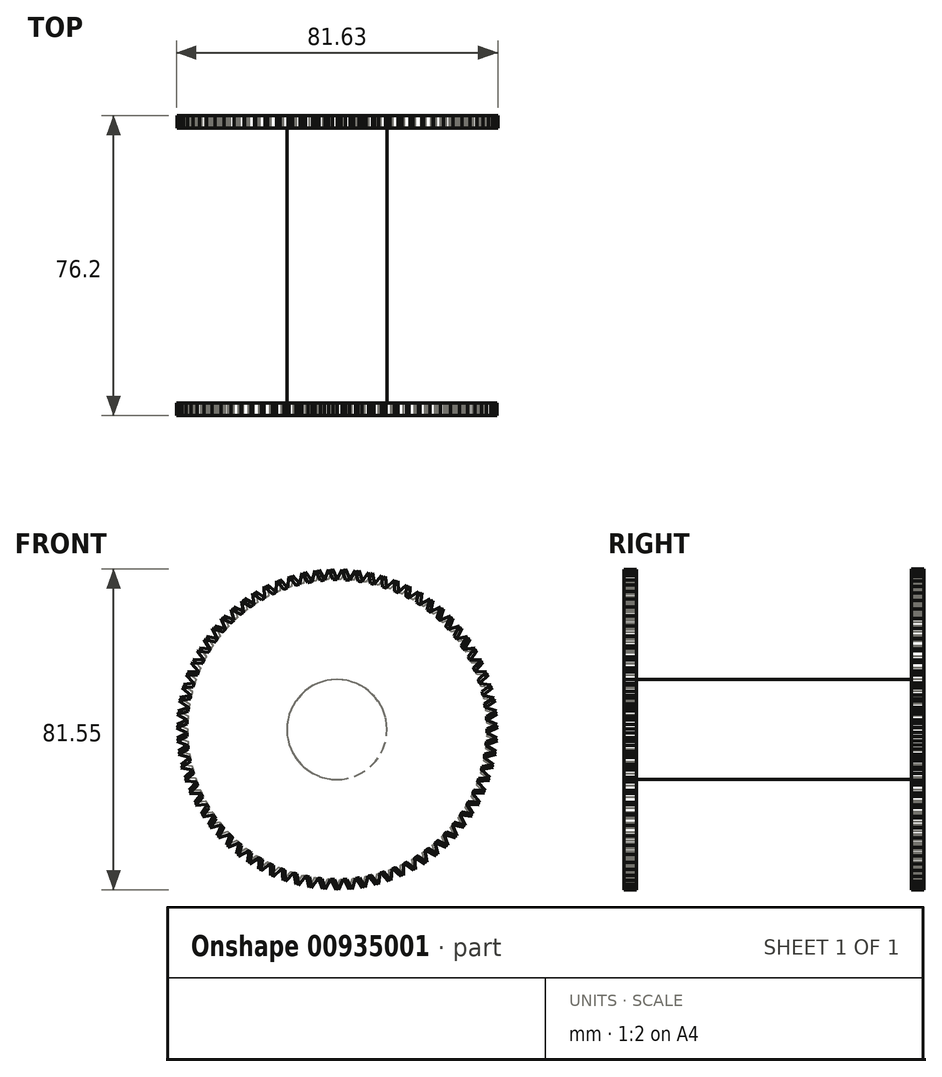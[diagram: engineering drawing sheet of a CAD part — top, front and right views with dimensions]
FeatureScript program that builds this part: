
annotation { "Feature Type Name" : "Feature", "Feature Type Description" : "" }
export const myFeature = defineFeature(function(context is Context, id is Id, definition is map)
    precondition{}
    {
        {
            var Q0;
            Q0=qCreatedBy(makeId("Front.planeOp"),FACE);
            var sketch = newSketch(context, id + "F0", { "sketchPlane" : qUnion([Q0])});
            skCircle(sketch, "E0", {"center": v(0, 0) * mm, "radius": 12.7 * mm});
            skSolve(sketch);
        }
        {
            var Q0;
            Q0 = qSketchRegion(id + "F0", true);
            extrude(context, id + "F1", {"entities" : qUnion([Q0]), "depth" : 69.85 * mm, "offsetDistance" : 25.4 * mm, "symmetric" : true});
        }
        {
            var Q0;
            Q0=makeQuery(id+"F1.opExtrude","CAP_FACE",FACE,{"disambiguationData":[OSD([sQuery(id+"F0.wireOp",EDGE,"E0")])],"isStart":false});
            var sketch = newSketch(context, id + "F2", { "sketchPlane" : qUnion([Q0])});
            skCircle(sketch, "E1", {"center": v(0, 0) * mm, "radius": 38.1 * mm});
            skLineSegment(sketch, "E2", {"start": v(0, 38.1) * mm, "end": v(1.3, 40.73) * mm});
            skLineSegment(sketch, "E3", {"start": v(1.3, 40.73) * mm, "end": v(2.24, 38.03) * mm});
            skLineSegment(sketch, "E4", {"start": v(2.24, 38.03) * mm, "end": v(0, 38.1) * mm});
            skLineSegment(sketch, "E5.1.0", {"start": v(-0.95, 38.09) * mm, "end": v(-3.19, 37.97) * mm});
            skLineSegment(sketch, "E5.1.1", {"start": v(-2.12, 40.7) * mm, "end": v(-0.95, 38.09) * mm});
            skLineSegment(sketch, "E5.1.2", {"start": v(-3.19, 37.97) * mm, "end": v(-2.12, 40.7) * mm});
            skLineSegment(sketch, "E5.2.0", {"start": v(-4.13, 37.88) * mm, "end": v(-6.35, 37.57) * mm});
            skLineSegment(sketch, "E5.2.1", {"start": v(-5.52, 40.37) * mm, "end": v(-4.13, 37.88) * mm});
            skLineSegment(sketch, "E5.2.2", {"start": v(-6.35, 37.57) * mm, "end": v(-5.52, 40.37) * mm});
            skLineSegment(sketch, "E5.3.0", {"start": v(-7.29, 37.4) * mm, "end": v(-9.48, 36.9) * mm});
            skLineSegment(sketch, "E5.3.1", {"start": v(-8.88, 39.77) * mm, "end": v(-7.29, 37.4) * mm});
            skLineSegment(sketch, "E5.3.2", {"start": v(-9.48, 36.9) * mm, "end": v(-8.88, 39.77) * mm});
            skLineSegment(sketch, "E5.4.0", {"start": v(-10.4, 36.66) * mm, "end": v(-12.53, 35.98) * mm});
            skLineSegment(sketch, "E5.4.1", {"start": v(-12.17, 38.89) * mm, "end": v(-10.4, 36.66) * mm});
            skLineSegment(sketch, "E5.4.2", {"start": v(-12.53, 35.98) * mm, "end": v(-12.17, 38.89) * mm});
            skLineSegment(sketch, "E5.5.0", {"start": v(-13.42, 35.66) * mm, "end": v(-15.5, 34.8) * mm});
            skLineSegment(sketch, "E5.5.1", {"start": v(-15.38, 37.73) * mm, "end": v(-13.42, 35.66) * mm});
            skLineSegment(sketch, "E5.5.2", {"start": v(-15.5, 34.8) * mm, "end": v(-15.38, 37.73) * mm});
            skLineSegment(sketch, "E5.6.0", {"start": v(-16.36, 34.4) * mm, "end": v(-18.35, 33.39) * mm});
            skLineSegment(sketch, "E5.6.1", {"start": v(-18.49, 36.31) * mm, "end": v(-16.36, 34.4) * mm});
            skLineSegment(sketch, "E5.6.2", {"start": v(-18.35, 33.39) * mm, "end": v(-18.49, 36.31) * mm});
            skLineSegment(sketch, "E5.7.0", {"start": v(-19.18, 32.92) * mm, "end": v(-21.08, 31.73) * mm});
            skLineSegment(sketch, "E5.7.1", {"start": v(-21.46, 34.64) * mm, "end": v(-19.18, 32.92) * mm});
            skLineSegment(sketch, "E5.7.2", {"start": v(-21.08, 31.73) * mm, "end": v(-21.46, 34.64) * mm});
            skLineSegment(sketch, "E5.8.0", {"start": v(-21.87, 31.2) * mm, "end": v(-23.67, 29.86) * mm});
            skLineSegment(sketch, "E5.8.1", {"start": v(-24.29, 32.72) * mm, "end": v(-21.87, 31.2) * mm});
            skLineSegment(sketch, "E5.8.2", {"start": v(-23.67, 29.86) * mm, "end": v(-24.29, 32.72) * mm});
            skLineSegment(sketch, "E5.9.0", {"start": v(-24.4, 29.26) * mm, "end": v(-26.08, 27.77) * mm});
            skLineSegment(sketch, "E5.9.1", {"start": v(-26.94, 30.58) * mm, "end": v(-24.4, 29.26) * mm});
            skLineSegment(sketch, "E5.9.2", {"start": v(-26.08, 27.77) * mm, "end": v(-26.94, 30.58) * mm});
            skLineSegment(sketch, "E5.10.0", {"start": v(-26.77, 27.11) * mm, "end": v(-28.31, 25.5) * mm});
            skLineSegment(sketch, "E5.10.1", {"start": v(-29.4, 28.21) * mm, "end": v(-26.77, 27.11) * mm});
            skLineSegment(sketch, "E5.10.2", {"start": v(-28.31, 25.5) * mm, "end": v(-29.4, 28.21) * mm});
            skLineSegment(sketch, "E5.11.0", {"start": v(-28.94, 24.78) * mm, "end": v(-30.35, 23.04) * mm});
            skLineSegment(sketch, "E5.11.1", {"start": v(-31.66, 25.66) * mm, "end": v(-28.94, 24.78) * mm});
            skLineSegment(sketch, "E5.11.2", {"start": v(-30.35, 23.04) * mm, "end": v(-31.66, 25.66) * mm});
            skLineSegment(sketch, "E5.12.0", {"start": v(-30.91, 22.27) * mm, "end": v(-32.17, 20.42) * mm});
            skLineSegment(sketch, "E5.12.1", {"start": v(-33.7, 22.92) * mm, "end": v(-30.91, 22.27) * mm});
            skLineSegment(sketch, "E5.12.2", {"start": v(-32.17, 20.42) * mm, "end": v(-33.7, 22.92) * mm});
            skLineSegment(sketch, "E5.13.0", {"start": v(-32.67, 19.6) * mm, "end": v(-33.76, 17.65) * mm});
            skLineSegment(sketch, "E5.13.1", {"start": v(-35.5, 20.02) * mm, "end": v(-32.67, 19.6) * mm});
            skLineSegment(sketch, "E5.13.2", {"start": v(-33.76, 17.65) * mm, "end": v(-35.5, 20.02) * mm});
            skLineSegment(sketch, "E5.14.0", {"start": v(-34.2, 16.8) * mm, "end": v(-35.12, 14.76) * mm});
            skLineSegment(sketch, "E5.14.1", {"start": v(-37.05, 16.98) * mm, "end": v(-34.2, 16.8) * mm});
            skLineSegment(sketch, "E5.14.2", {"start": v(-35.12, 14.76) * mm, "end": v(-37.05, 16.98) * mm});
            skLineSegment(sketch, "E5.15.0", {"start": v(-35.48, 13.88) * mm, "end": v(-36.24, 11.77) * mm});
            skLineSegment(sketch, "E5.15.1", {"start": v(-38.34, 13.82) * mm, "end": v(-35.48, 13.88) * mm});
            skLineSegment(sketch, "E5.15.2", {"start": v(-36.24, 11.77) * mm, "end": v(-38.34, 13.82) * mm});
            skLineSegment(sketch, "E5.16.0", {"start": v(-36.52, 10.87) * mm, "end": v(-37.1, 8.7) * mm});
            skLineSegment(sketch, "E5.16.1", {"start": v(-39.36, 10.56) * mm, "end": v(-36.52, 10.87) * mm});
            skLineSegment(sketch, "E5.16.2", {"start": v(-37.1, 8.7) * mm, "end": v(-39.36, 10.56) * mm});
            skLineSegment(sketch, "E5.17.0", {"start": v(-37.3, 7.77) * mm, "end": v(-37.7, 5.57) * mm});
            skLineSegment(sketch, "E5.17.1", {"start": v(-40.1, 7.23) * mm, "end": v(-37.3, 7.77) * mm});
            skLineSegment(sketch, "E5.17.2", {"start": v(-37.7, 5.57) * mm, "end": v(-40.1, 7.23) * mm});
            skLineSegment(sketch, "E5.18.0", {"start": v(-37.82, 4.62) * mm, "end": v(-38.02, 2.4) * mm});
            skLineSegment(sketch, "E5.18.1", {"start": v(-40.57, 3.85) * mm, "end": v(-37.82, 4.62) * mm});
            skLineSegment(sketch, "E5.18.2", {"start": v(-38.02, 2.4) * mm, "end": v(-40.57, 3.85) * mm});
            skLineSegment(sketch, "E5.19.0", {"start": v(-38.07, 1.44) * mm, "end": v(-38.1, -0.8) * mm});
            skLineSegment(sketch, "E5.19.1", {"start": v(-40.75, 0.44) * mm, "end": v(-38.07, 1.44) * mm});
            skLineSegment(sketch, "E5.19.2", {"start": v(-38.1, -0.8) * mm, "end": v(-40.75, 0.44) * mm});
            skLineSegment(sketch, "E6.1.20.0", {"start": v(-38.06, -1.75) * mm, "end": v(-37.9, -3.98) * mm});
            skLineSegment(sketch, "E6.3.20.0", {"start": v(-40.64, -2.97) * mm, "end": v(-38.06, -1.75) * mm});
            skLineSegment(sketch, "E6.6.20.0", {"start": v(-37.9, -3.98) * mm, "end": v(-40.64, -2.97) * mm});
            skLineSegment(sketch, "E6.1.21.0", {"start": v(-37.78, -4.93) * mm, "end": v(-37.43, -7.14) * mm});
            skLineSegment(sketch, "E6.3.21.0", {"start": v(-40.25, -6.36) * mm, "end": v(-37.78, -4.93) * mm});
            skLineSegment(sketch, "E6.6.21.0", {"start": v(-37.43, -7.14) * mm, "end": v(-40.25, -6.36) * mm});
            skLineSegment(sketch, "E6.1.22.0", {"start": v(-37.24, -8.07) * mm, "end": v(-36.7, -10.25) * mm});
            skLineSegment(sketch, "E6.3.22.0", {"start": v(-39.58, -9.7) * mm, "end": v(-37.24, -8.07) * mm});
            skLineSegment(sketch, "E6.6.22.0", {"start": v(-36.7, -10.25) * mm, "end": v(-39.58, -9.7) * mm});
            skLineSegment(sketch, "E6.1.23.0", {"start": v(-36.43, -11.16) * mm, "end": v(-35.71, -13.28) * mm});
            skLineSegment(sketch, "E6.3.23.0", {"start": v(-38.63, -12.98) * mm, "end": v(-36.43, -11.16) * mm});
            skLineSegment(sketch, "E6.6.23.0", {"start": v(-35.71, -13.28) * mm, "end": v(-38.63, -12.98) * mm});
            skLineSegment(sketch, "E6.1.24.0", {"start": v(-35.37, -14.17) * mm, "end": v(-34.47, -16.22) * mm});
            skLineSegment(sketch, "E6.3.24.0", {"start": v(-37.4, -16.17) * mm, "end": v(-35.37, -14.17) * mm});
            skLineSegment(sketch, "E6.6.24.0", {"start": v(-34.47, -16.22) * mm, "end": v(-37.4, -16.17) * mm});
            skLineSegment(sketch, "E6.1.25.0", {"start": v(-34.06, -17.08) * mm, "end": v(-33, -19.05) * mm});
            skLineSegment(sketch, "E6.3.25.0", {"start": v(-35.92, -19.24) * mm, "end": v(-34.06, -17.08) * mm});
            skLineSegment(sketch, "E6.6.25.0", {"start": v(-33, -19.05) * mm, "end": v(-35.92, -19.24) * mm});
            skLineSegment(sketch, "E6.1.26.0", {"start": v(-32.51, -19.87) * mm, "end": v(-31.29, -21.74) * mm});
            skLineSegment(sketch, "E6.3.26.0", {"start": v(-34.18, -22.18) * mm, "end": v(-32.51, -19.87) * mm});
            skLineSegment(sketch, "E6.6.26.0", {"start": v(-31.29, -21.74) * mm, "end": v(-34.18, -22.18) * mm});
            skLineSegment(sketch, "E6.1.27.0", {"start": v(-30.73, -22.52) * mm, "end": v(-29.36, -24.29) * mm});
            skLineSegment(sketch, "E6.3.27.0", {"start": v(-32.2, -24.97) * mm, "end": v(-30.73, -22.52) * mm});
            skLineSegment(sketch, "E6.6.27.0", {"start": v(-29.36, -24.29) * mm, "end": v(-32.2, -24.97) * mm});
            skLineSegment(sketch, "E6.1.28.0", {"start": v(-28.74, -25.01) * mm, "end": v(-27.22, -26.66) * mm});
            skLineSegment(sketch, "E6.3.28.0", {"start": v(-30, -27.57) * mm, "end": v(-28.74, -25.01) * mm});
            skLineSegment(sketch, "E6.6.28.0", {"start": v(-27.22, -26.66) * mm, "end": v(-30, -27.57) * mm});
            skLineSegment(sketch, "E6.1.29.0", {"start": v(-26.55, -27.33) * mm, "end": v(-24.9, -28.84) * mm});
            skLineSegment(sketch, "E6.3.29.0", {"start": v(-27.6, -29.99) * mm, "end": v(-26.55, -27.33) * mm});
            skLineSegment(sketch, "E6.6.29.0", {"start": v(-24.9, -28.84) * mm, "end": v(-27.6, -29.99) * mm});
            skLineSegment(sketch, "E6.1.30.0", {"start": v(-24.17, -29.45) * mm, "end": v(-22.4, -30.82) * mm});
            skLineSegment(sketch, "E6.3.30.0", {"start": v(-24.99, -32.2) * mm, "end": v(-24.17, -29.45) * mm});
            skLineSegment(sketch, "E6.6.30.0", {"start": v(-22.4, -30.82) * mm, "end": v(-24.99, -32.2) * mm});
            skLineSegment(sketch, "E6.1.31.0", {"start": v(-21.62, -31.37) * mm, "end": v(-19.74, -32.59) * mm});
            skLineSegment(sketch, "E6.3.31.0", {"start": v(-22.2, -34.17) * mm, "end": v(-21.62, -31.37) * mm});
            skLineSegment(sketch, "E6.6.31.0", {"start": v(-19.74, -32.59) * mm, "end": v(-22.2, -34.17) * mm});
            skLineSegment(sketch, "E6.1.32.0", {"start": v(-18.92, -33.07) * mm, "end": v(-16.94, -34.13) * mm});
            skLineSegment(sketch, "E6.3.32.0", {"start": v(-19.27, -35.9) * mm, "end": v(-18.92, -33.07) * mm});
            skLineSegment(sketch, "E6.6.32.0", {"start": v(-16.94, -34.13) * mm, "end": v(-19.27, -35.9) * mm});
            skLineSegment(sketch, "E6.1.33.0", {"start": v(-16.08, -34.54) * mm, "end": v(-14.03, -35.42) * mm});
            skLineSegment(sketch, "E6.3.33.0", {"start": v(-16.2, -37.4) * mm, "end": v(-16.08, -34.54) * mm});
            skLineSegment(sketch, "E6.6.33.0", {"start": v(-14.03, -35.42) * mm, "end": v(-16.2, -37.4) * mm});
            skLineSegment(sketch, "E6.1.34.0", {"start": v(-13.14, -35.76) * mm, "end": v(-11.01, -36.47) * mm});
            skLineSegment(sketch, "E6.3.34.0", {"start": v(-13.01, -38.62) * mm, "end": v(-13.14, -35.76) * mm});
            skLineSegment(sketch, "E6.6.34.0", {"start": v(-11.01, -36.47) * mm, "end": v(-13.01, -38.62) * mm});
            skLineSegment(sketch, "E6.1.35.0", {"start": v(-10.1, -36.74) * mm, "end": v(-7.92, -37.27) * mm});
            skLineSegment(sketch, "E6.3.35.0", {"start": v(-9.73, -39.57) * mm, "end": v(-10.1, -36.74) * mm});
            skLineSegment(sketch, "E6.6.35.0", {"start": v(-7.92, -37.27) * mm, "end": v(-9.73, -39.57) * mm});
            skLineSegment(sketch, "E6.1.36.0", {"start": v(-6.99, -37.45) * mm, "end": v(-4.78, -37.8) * mm});
            skLineSegment(sketch, "E6.3.36.0", {"start": v(-6.39, -40.25) * mm, "end": v(-6.99, -37.45) * mm});
            skLineSegment(sketch, "E6.6.36.0", {"start": v(-4.78, -37.8) * mm, "end": v(-6.39, -40.25) * mm});
            skLineSegment(sketch, "E6.1.37.0", {"start": v(-3.83, -37.9) * mm, "end": v(-1.6, -38.07) * mm});
            skLineSegment(sketch, "E6.3.37.0", {"start": v(-3, -40.64) * mm, "end": v(-3.83, -37.9) * mm});
            skLineSegment(sketch, "E6.6.37.0", {"start": v(-1.6, -38.07) * mm, "end": v(-3, -40.64) * mm});
            skLineSegment(sketch, "E6.1.38.0", {"start": v(-0.65, -38.1) * mm, "end": v(1.6, -38.07) * mm});
            skLineSegment(sketch, "E6.3.38.0", {"start": v(0.41, -40.75) * mm, "end": v(-0.65, -38.1) * mm});
            skLineSegment(sketch, "E6.6.38.0", {"start": v(1.6, -38.07) * mm, "end": v(0.41, -40.75) * mm});
            skLineSegment(sketch, "E6.1.39.0", {"start": v(2.54, -38.01) * mm, "end": v(4.78, -37.8) * mm});
            skLineSegment(sketch, "E6.3.39.0", {"start": v(3.82, -40.57) * mm, "end": v(2.54, -38.01) * mm});
            skLineSegment(sketch, "E6.6.39.0", {"start": v(4.78, -37.8) * mm, "end": v(3.82, -40.57) * mm});
            skLineSegment(sketch, "E6.1.40.0", {"start": v(5.72, -37.67) * mm, "end": v(7.92, -37.27) * mm});
            skLineSegment(sketch, "E6.3.40.0", {"start": v(7.2, -40.1) * mm, "end": v(5.72, -37.67) * mm});
            skLineSegment(sketch, "E6.6.40.0", {"start": v(7.92, -37.27) * mm, "end": v(7.2, -40.1) * mm});
            skLineSegment(sketch, "E6.1.41.0", {"start": v(8.85, -37.06) * mm, "end": v(11.01, -36.47) * mm});
            skLineSegment(sketch, "E6.3.41.0", {"start": v(10.53, -39.37) * mm, "end": v(8.85, -37.06) * mm});
            skLineSegment(sketch, "E6.6.41.0", {"start": v(11.01, -36.47) * mm, "end": v(10.53, -39.37) * mm});
            skLineSegment(sketch, "E6.1.42.0", {"start": v(11.92, -36.19) * mm, "end": v(14.03, -35.42) * mm});
            skLineSegment(sketch, "E6.3.42.0", {"start": v(13.8, -38.35) * mm, "end": v(11.92, -36.19) * mm});
            skLineSegment(sketch, "E6.6.42.0", {"start": v(14.03, -35.42) * mm, "end": v(13.8, -38.35) * mm});
            skLineSegment(sketch, "E6.1.43.0", {"start": v(14.9, -35.06) * mm, "end": v(16.94, -34.13) * mm});
            skLineSegment(sketch, "E6.3.43.0", {"start": v(16.95, -37.06) * mm, "end": v(14.9, -35.06) * mm});
            skLineSegment(sketch, "E6.6.43.0", {"start": v(16.94, -34.13) * mm, "end": v(16.95, -37.06) * mm});
            skLineSegment(sketch, "E6.1.44.0", {"start": v(17.79, -33.7) * mm, "end": v(19.74, -32.59) * mm});
            skLineSegment(sketch, "E6.3.44.0", {"start": v(20, -35.5) * mm, "end": v(17.79, -33.7) * mm});
            skLineSegment(sketch, "E6.6.44.0", {"start": v(19.74, -32.59) * mm, "end": v(20, -35.5) * mm});
            skLineSegment(sketch, "E6.1.45.0", {"start": v(20.54, -32.09) * mm, "end": v(22.4, -30.82) * mm});
            skLineSegment(sketch, "E6.3.45.0", {"start": v(22.9, -33.71) * mm, "end": v(20.54, -32.09) * mm});
            skLineSegment(sketch, "E6.6.45.0", {"start": v(22.4, -30.82) * mm, "end": v(22.9, -33.71) * mm});
            skLineSegment(sketch, "E6.1.46.0", {"start": v(23.16, -30.26) * mm, "end": v(24.9, -28.84) * mm});
            skLineSegment(sketch, "E6.3.46.0", {"start": v(25.63, -31.68) * mm, "end": v(23.16, -30.26) * mm});
            skLineSegment(sketch, "E6.6.46.0", {"start": v(24.9, -28.84) * mm, "end": v(25.63, -31.68) * mm});
            skLineSegment(sketch, "E6.1.47.0", {"start": v(25.6, -28.21) * mm, "end": v(27.22, -26.66) * mm});
            skLineSegment(sketch, "E6.3.47.0", {"start": v(28.2, -29.42) * mm, "end": v(25.6, -28.21) * mm});
            skLineSegment(sketch, "E6.6.47.0", {"start": v(27.22, -26.66) * mm, "end": v(28.2, -29.42) * mm});
            skLineSegment(sketch, "E6.1.48.0", {"start": v(27.88, -25.97) * mm, "end": v(29.36, -24.29) * mm});
            skLineSegment(sketch, "E6.3.48.0", {"start": v(30.56, -26.96) * mm, "end": v(27.88, -25.97) * mm});
            skLineSegment(sketch, "E6.6.48.0", {"start": v(29.36, -24.29) * mm, "end": v(30.56, -26.96) * mm});
            skLineSegment(sketch, "E6.1.49.0", {"start": v(29.95, -23.55) * mm, "end": v(31.29, -21.74) * mm});
            skLineSegment(sketch, "E6.3.49.0", {"start": v(32.7, -24.3) * mm, "end": v(29.95, -23.55) * mm});
            skLineSegment(sketch, "E6.6.49.0", {"start": v(31.29, -21.74) * mm, "end": v(32.7, -24.3) * mm});
            skLineSegment(sketch, "E7.1.50.0", {"start": v(31.82, -20.96) * mm, "end": v(33, -19.05) * mm});
            skLineSegment(sketch, "E7.3.50.0", {"start": v(34.63, -21.49) * mm, "end": v(31.82, -20.96) * mm});
            skLineSegment(sketch, "E7.6.50.0", {"start": v(33, -19.05) * mm, "end": v(34.63, -21.49) * mm});
            skLineSegment(sketch, "E7.1.51.0", {"start": v(33.46, -18.22) * mm, "end": v(34.47, -16.22) * mm});
            skLineSegment(sketch, "E7.3.51.0", {"start": v(36.3, -18.51) * mm, "end": v(33.46, -18.22) * mm});
            skLineSegment(sketch, "E7.6.51.0", {"start": v(34.47, -16.22) * mm, "end": v(36.3, -18.51) * mm});
            skLineSegment(sketch, "E7.1.52.0", {"start": v(34.87, -15.36) * mm, "end": v(35.71, -13.28) * mm});
            skLineSegment(sketch, "E7.3.52.0", {"start": v(37.72, -15.4) * mm, "end": v(34.87, -15.36) * mm});
            skLineSegment(sketch, "E7.6.52.0", {"start": v(35.71, -13.28) * mm, "end": v(37.72, -15.4) * mm});
            skLineSegment(sketch, "E7.1.53.0", {"start": v(36.03, -12.39) * mm, "end": v(36.7, -10.25) * mm});
            skLineSegment(sketch, "E7.3.53.0", {"start": v(38.88, -12.2) * mm, "end": v(36.03, -12.39) * mm});
            skLineSegment(sketch, "E7.6.53.0", {"start": v(36.7, -10.25) * mm, "end": v(38.88, -12.2) * mm});
            skLineSegment(sketch, "E7.1.54.0", {"start": v(36.94, -9.33) * mm, "end": v(37.43, -7.14) * mm});
            skLineSegment(sketch, "E7.3.54.0", {"start": v(39.77, -8.9) * mm, "end": v(36.94, -9.33) * mm});
            skLineSegment(sketch, "E7.6.54.0", {"start": v(37.43, -7.14) * mm, "end": v(39.77, -8.9) * mm});
            skLineSegment(sketch, "E7.1.55.0", {"start": v(37.6, -6.2) * mm, "end": v(37.9, -3.98) * mm});
            skLineSegment(sketch, "E7.3.55.0", {"start": v(40.37, -5.54) * mm, "end": v(37.6, -6.2) * mm});
            skLineSegment(sketch, "E7.6.55.0", {"start": v(37.9, -3.98) * mm, "end": v(40.37, -5.54) * mm});
            skLineSegment(sketch, "E7.1.56.0", {"start": v(37.98, -3.04) * mm, "end": v(38.1, -0.8) * mm});
            skLineSegment(sketch, "E7.3.56.0", {"start": v(40.7, -2.15) * mm, "end": v(37.98, -3.04) * mm});
            skLineSegment(sketch, "E7.6.56.0", {"start": v(38.1, -0.8) * mm, "end": v(40.7, -2.15) * mm});
            skLineSegment(sketch, "E7.1.57.0", {"start": v(38.1, 0.15) * mm, "end": v(38.02, 2.4) * mm});
            skLineSegment(sketch, "E7.3.57.0", {"start": v(40.73, 1.27) * mm, "end": v(38.1, 0.15) * mm});
            skLineSegment(sketch, "E7.6.57.0", {"start": v(38.02, 2.4) * mm, "end": v(40.73, 1.27) * mm});
            skLineSegment(sketch, "E7.1.58.0", {"start": v(37.95, 3.34) * mm, "end": v(37.7, 5.57) * mm});
            skLineSegment(sketch, "E7.3.58.0", {"start": v(40.48, 4.67) * mm, "end": v(37.95, 3.34) * mm});
            skLineSegment(sketch, "E7.6.58.0", {"start": v(37.7, 5.57) * mm, "end": v(40.48, 4.67) * mm});
            skLineSegment(sketch, "E7.1.59.0", {"start": v(37.54, 6.5) * mm, "end": v(37.1, 8.7) * mm});
            skLineSegment(sketch, "E7.3.59.0", {"start": v(39.95, 8.04) * mm, "end": v(37.54, 6.5) * mm});
            skLineSegment(sketch, "E7.6.59.0", {"start": v(37.1, 8.7) * mm, "end": v(39.95, 8.04) * mm});
            skLineSegment(sketch, "E7.1.60.0", {"start": v(36.86, 9.62) * mm, "end": v(36.24, 11.77) * mm});
            skLineSegment(sketch, "E7.3.60.0", {"start": v(39.14, 11.36) * mm, "end": v(36.86, 9.62) * mm});
            skLineSegment(sketch, "E7.6.60.0", {"start": v(36.24, 11.77) * mm, "end": v(39.14, 11.36) * mm});
            skLineSegment(sketch, "E7.1.61.0", {"start": v(35.93, 12.67) * mm, "end": v(35.12, 14.76) * mm});
            skLineSegment(sketch, "E7.3.61.0", {"start": v(38.05, 14.6) * mm, "end": v(35.93, 12.67) * mm});
            skLineSegment(sketch, "E7.6.61.0", {"start": v(35.12, 14.76) * mm, "end": v(38.05, 14.6) * mm});
            skLineSegment(sketch, "E7.1.62.0", {"start": v(34.74, 15.64) * mm, "end": v(33.76, 17.65) * mm});
            skLineSegment(sketch, "E7.3.62.0", {"start": v(36.7, 17.72) * mm, "end": v(34.74, 15.64) * mm});
            skLineSegment(sketch, "E7.6.62.0", {"start": v(33.76, 17.65) * mm, "end": v(36.7, 17.72) * mm});
            skLineSegment(sketch, "E7.1.63.0", {"start": v(33.31, 18.49) * mm, "end": v(32.17, 20.42) * mm});
            skLineSegment(sketch, "E7.3.63.0", {"start": v(35.08, 20.73) * mm, "end": v(33.31, 18.49) * mm});
            skLineSegment(sketch, "E7.6.63.0", {"start": v(32.17, 20.42) * mm, "end": v(35.08, 20.73) * mm});
            skLineSegment(sketch, "E7.1.64.0", {"start": v(31.65, 21.21) * mm, "end": v(30.35, 23.04) * mm});
            skLineSegment(sketch, "E7.3.64.0", {"start": v(33.22, 23.6) * mm, "end": v(31.65, 21.21) * mm});
            skLineSegment(sketch, "E7.6.64.0", {"start": v(30.35, 23.04) * mm, "end": v(33.22, 23.6) * mm});
            skLineSegment(sketch, "E7.1.65.0", {"start": v(29.76, 23.78) * mm, "end": v(28.31, 25.5) * mm});
            skLineSegment(sketch, "E7.3.65.0", {"start": v(31.13, 26.3) * mm, "end": v(29.76, 23.78) * mm});
            skLineSegment(sketch, "E7.6.65.0", {"start": v(28.31, 25.5) * mm, "end": v(31.13, 26.3) * mm});
            skLineSegment(sketch, "E7.1.66.0", {"start": v(27.67, 26.2) * mm, "end": v(26.08, 27.77) * mm});
            skLineSegment(sketch, "E7.3.66.0", {"start": v(28.82, 28.8) * mm, "end": v(27.67, 26.2) * mm});
            skLineSegment(sketch, "E7.6.66.0", {"start": v(26.08, 27.77) * mm, "end": v(28.82, 28.8) * mm});
            skLineSegment(sketch, "E7.1.67.0", {"start": v(25.38, 28.42) * mm, "end": v(23.67, 29.86) * mm});
            skLineSegment(sketch, "E7.3.67.0", {"start": v(26.31, 31.12) * mm, "end": v(25.38, 28.42) * mm});
            skLineSegment(sketch, "E7.6.67.0", {"start": v(23.67, 29.86) * mm, "end": v(26.31, 31.12) * mm});
            skLineSegment(sketch, "E7.1.68.0", {"start": v(22.91, 30.44) * mm, "end": v(21.08, 31.73) * mm});
            skLineSegment(sketch, "E7.3.68.0", {"start": v(23.62, 33.2) * mm, "end": v(22.91, 30.44) * mm});
            skLineSegment(sketch, "E7.6.68.0", {"start": v(21.08, 31.73) * mm, "end": v(23.62, 33.2) * mm});
            skLineSegment(sketch, "E7.1.69.0", {"start": v(20.29, 32.25) * mm, "end": v(18.35, 33.39) * mm});
            skLineSegment(sketch, "E7.3.69.0", {"start": v(20.76, 35.07) * mm, "end": v(20.29, 32.25) * mm});
            skLineSegment(sketch, "E7.6.69.0", {"start": v(18.35, 33.39) * mm, "end": v(20.76, 35.07) * mm});
            skLineSegment(sketch, "E7.1.70.0", {"start": v(17.52, 33.83) * mm, "end": v(15.5, 34.8) * mm});
            skLineSegment(sketch, "E7.3.70.0", {"start": v(17.75, 36.68) * mm, "end": v(17.52, 33.83) * mm});
            skLineSegment(sketch, "E7.6.70.0", {"start": v(15.5, 34.8) * mm, "end": v(17.75, 36.68) * mm});
            skLineSegment(sketch, "E7.1.71.0", {"start": v(14.62, 35.18) * mm, "end": v(12.53, 35.98) * mm});
            skLineSegment(sketch, "E7.3.71.0", {"start": v(14.62, 38.04) * mm, "end": v(14.62, 35.18) * mm});
            skLineSegment(sketch, "E7.6.71.0", {"start": v(12.53, 35.98) * mm, "end": v(14.62, 38.04) * mm});
            skLineSegment(sketch, "E7.1.72.0", {"start": v(11.63, 36.28) * mm, "end": v(9.48, 36.9) * mm});
            skLineSegment(sketch, "E7.3.72.0", {"start": v(11.38, 39.13) * mm, "end": v(11.63, 36.28) * mm});
            skLineSegment(sketch, "E7.6.72.0", {"start": v(9.48, 36.9) * mm, "end": v(11.38, 39.13) * mm});
            skLineSegment(sketch, "E7.1.73.0", {"start": v(8.55, 37.13) * mm, "end": v(6.35, 37.57) * mm});
            skLineSegment(sketch, "E7.3.73.0", {"start": v(8.07, 39.94) * mm, "end": v(8.55, 37.13) * mm});
            skLineSegment(sketch, "E7.6.73.0", {"start": v(6.35, 37.57) * mm, "end": v(8.07, 39.94) * mm});
            skLineSegment(sketch, "E7.1.74.0", {"start": v(5.41, 37.71) * mm, "end": v(3.19, 37.97) * mm});
            skLineSegment(sketch, "E7.3.74.0", {"start": v(4.7, 40.48) * mm, "end": v(5.41, 37.71) * mm});
            skLineSegment(sketch, "E7.6.74.0", {"start": v(3.19, 37.97) * mm, "end": v(4.7, 40.48) * mm});
            skSolve(sketch);
        }
        {
            var Q0;
            Q0 = qSketchRegion(id + "F2", true);
            extrude(context, id + "F3", {"entities" : qUnion([Q0]), "operationType" : NewBodyOperationType.ADD, "depth" : 3.17 * mm, "offsetDistance" : 25.4 * mm});
        }
        {
            var Q0;
            Q0=makeQuery(id+"F1.opExtrude","CAP_FACE",FACE,{"disambiguationData":[OSD([sQuery(id+"F0.wireOp",EDGE,"E0")])],"isStart":true});
            var sketch = newSketch(context, id + "F4", { "sketchPlane" : qUnion([Q0])});
            skCircle(sketch, "E8", {"center": v(-0.13, 0.07) * mm, "radius": 38.1 * mm});
            skLineSegment(sketch, "E9", {"start": v(-0.13, 38.17) * mm, "end": v(1.16, 40.8) * mm});
            skLineSegment(sketch, "E10", {"start": v(1.16, 40.8) * mm, "end": v(2.1, 38.1) * mm});
            skLineSegment(sketch, "E11", {"start": v(2.1, 38.1) * mm, "end": v(-0.13, 38.17) * mm});
            skLineSegment(sketch, "E12.1.0", {"start": v(-1.08, 38.15) * mm, "end": v(-3.32, 38.03) * mm});
            skLineSegment(sketch, "E12.1.1", {"start": v(-2.25, 40.76) * mm, "end": v(-1.08, 38.15) * mm});
            skLineSegment(sketch, "E12.1.2", {"start": v(-3.32, 38.03) * mm, "end": v(-2.25, 40.76) * mm});
            skLineSegment(sketch, "E12.2.0", {"start": v(-4.27, 37.94) * mm, "end": v(-6.49, 37.63) * mm});
            skLineSegment(sketch, "E12.2.1", {"start": v(-5.65, 40.44) * mm, "end": v(-4.27, 37.94) * mm});
            skLineSegment(sketch, "E12.2.2", {"start": v(-6.49, 37.63) * mm, "end": v(-5.65, 40.44) * mm});
            skLineSegment(sketch, "E12.3.0", {"start": v(-7.42, 37.46) * mm, "end": v(-9.6, 36.97) * mm});
            skLineSegment(sketch, "E12.3.1", {"start": v(-9, 39.84) * mm, "end": v(-7.42, 37.46) * mm});
            skLineSegment(sketch, "E12.3.2", {"start": v(-9.6, 36.97) * mm, "end": v(-9, 39.84) * mm});
            skLineSegment(sketch, "E12.4.0", {"start": v(-10.52, 36.72) * mm, "end": v(-12.66, 36.05) * mm});
            skLineSegment(sketch, "E12.4.1", {"start": v(-12.3, 38.96) * mm, "end": v(-10.52, 36.72) * mm});
            skLineSegment(sketch, "E12.4.2", {"start": v(-12.66, 36.05) * mm, "end": v(-12.3, 38.96) * mm});
            skLineSegment(sketch, "E12.5.0", {"start": v(-13.56, 35.72) * mm, "end": v(-15.63, 34.87) * mm});
            skLineSegment(sketch, "E12.5.1", {"start": v(-15.52, 37.8) * mm, "end": v(-13.56, 35.72) * mm});
            skLineSegment(sketch, "E12.5.2", {"start": v(-15.63, 34.87) * mm, "end": v(-15.52, 37.8) * mm});
            skLineSegment(sketch, "E12.6.0", {"start": v(-16.5, 34.47) * mm, "end": v(-18.49, 33.45) * mm});
            skLineSegment(sketch, "E12.6.1", {"start": v(-18.62, 36.38) * mm, "end": v(-16.5, 34.47) * mm});
            skLineSegment(sketch, "E12.6.2", {"start": v(-18.49, 33.45) * mm, "end": v(-18.62, 36.38) * mm});
            skLineSegment(sketch, "E12.7.0", {"start": v(-19.31, 32.99) * mm, "end": v(-21.22, 31.8) * mm});
            skLineSegment(sketch, "E12.7.1", {"start": v(-21.6, 34.7) * mm, "end": v(-19.31, 32.99) * mm});
            skLineSegment(sketch, "E12.7.2", {"start": v(-21.22, 31.8) * mm, "end": v(-21.6, 34.7) * mm});
            skLineSegment(sketch, "E12.8.0", {"start": v(-22, 31.26) * mm, "end": v(-23.8, 29.92) * mm});
            skLineSegment(sketch, "E12.8.1", {"start": v(-24.42, 32.79) * mm, "end": v(-22, 31.26) * mm});
            skLineSegment(sketch, "E12.8.2", {"start": v(-23.8, 29.92) * mm, "end": v(-24.42, 32.79) * mm});
            skLineSegment(sketch, "E12.9.0", {"start": v(-24.53, 29.33) * mm, "end": v(-26.21, 27.84) * mm});
            skLineSegment(sketch, "E12.9.1", {"start": v(-27.07, 30.64) * mm, "end": v(-24.53, 29.33) * mm});
            skLineSegment(sketch, "E12.9.2", {"start": v(-26.21, 27.84) * mm, "end": v(-27.07, 30.64) * mm});
            skLineSegment(sketch, "E12.10.0", {"start": v(-26.9, 27.18) * mm, "end": v(-28.45, 25.56) * mm});
            skLineSegment(sketch, "E12.10.1", {"start": v(-29.53, 28.28) * mm, "end": v(-26.9, 27.18) * mm});
            skLineSegment(sketch, "E12.10.2", {"start": v(-28.45, 25.56) * mm, "end": v(-29.53, 28.28) * mm});
            skLineSegment(sketch, "E12.11.0", {"start": v(-29.07, 24.85) * mm, "end": v(-30.48, 23.1) * mm});
            skLineSegment(sketch, "E12.11.1", {"start": v(-31.8, 25.72) * mm, "end": v(-29.07, 24.85) * mm});
            skLineSegment(sketch, "E12.11.2", {"start": v(-30.48, 23.1) * mm, "end": v(-31.8, 25.72) * mm});
            skLineSegment(sketch, "E12.12.0", {"start": v(-31.04, 22.34) * mm, "end": v(-32.3, 20.48) * mm});
            skLineSegment(sketch, "E12.12.1", {"start": v(-33.83, 22.98) * mm, "end": v(-31.04, 22.34) * mm});
            skLineSegment(sketch, "E12.12.2", {"start": v(-32.3, 20.48) * mm, "end": v(-33.83, 22.98) * mm});
            skLineSegment(sketch, "E12.13.0", {"start": v(-32.8, 19.67) * mm, "end": v(-33.9, 17.72) * mm});
            skLineSegment(sketch, "E12.13.1", {"start": v(-35.63, 20.08) * mm, "end": v(-32.8, 19.67) * mm});
            skLineSegment(sketch, "E12.13.2", {"start": v(-33.9, 17.72) * mm, "end": v(-35.63, 20.08) * mm});
            skLineSegment(sketch, "E12.14.0", {"start": v(-34.33, 16.87) * mm, "end": v(-35.25, 14.83) * mm});
            skLineSegment(sketch, "E12.14.1", {"start": v(-37.18, 17.04) * mm, "end": v(-34.33, 16.87) * mm});
            skLineSegment(sketch, "E12.14.2", {"start": v(-35.25, 14.83) * mm, "end": v(-37.18, 17.04) * mm});
            skLineSegment(sketch, "E12.15.0", {"start": v(-35.61, 13.95) * mm, "end": v(-36.37, 11.84) * mm});
            skLineSegment(sketch, "E12.15.1", {"start": v(-38.47, 13.88) * mm, "end": v(-35.61, 13.95) * mm});
            skLineSegment(sketch, "E12.15.2", {"start": v(-36.37, 11.84) * mm, "end": v(-38.47, 13.88) * mm});
            skLineSegment(sketch, "E12.16.0", {"start": v(-36.65, 10.93) * mm, "end": v(-37.23, 8.77) * mm});
            skLineSegment(sketch, "E12.16.1", {"start": v(-39.49, 10.63) * mm, "end": v(-36.65, 10.93) * mm});
            skLineSegment(sketch, "E12.16.2", {"start": v(-37.23, 8.77) * mm, "end": v(-39.49, 10.63) * mm});
            skLineSegment(sketch, "E12.17.0", {"start": v(-37.43, 7.84) * mm, "end": v(-37.82, 5.63) * mm});
            skLineSegment(sketch, "E12.17.1", {"start": v(-40.24, 7.3) * mm, "end": v(-37.43, 7.84) * mm});
            skLineSegment(sketch, "E12.17.2", {"start": v(-37.82, 5.63) * mm, "end": v(-40.24, 7.3) * mm});
            skLineSegment(sketch, "E12.18.0", {"start": v(-37.95, 4.69) * mm, "end": v(-38.16, 2.46) * mm});
            skLineSegment(sketch, "E12.18.1", {"start": v(-40.7, 3.91) * mm, "end": v(-37.95, 4.69) * mm});
            skLineSegment(sketch, "E12.18.2", {"start": v(-38.16, 2.46) * mm, "end": v(-40.7, 3.91) * mm});
            skLineSegment(sketch, "E12.19.0", {"start": v(-38.2, 1.5) * mm, "end": v(-38.22, -0.73) * mm});
            skLineSegment(sketch, "E12.19.1", {"start": v(-40.88, 0.5) * mm, "end": v(-38.2, 1.5) * mm});
            skLineSegment(sketch, "E12.19.2", {"start": v(-38.22, -0.73) * mm, "end": v(-40.88, 0.5) * mm});
            skLineSegment(sketch, "E13.1.20.0", {"start": v(-38.2, -1.68) * mm, "end": v(-38.02, -3.92) * mm});
            skLineSegment(sketch, "E13.3.20.0", {"start": v(-40.77, -2.9) * mm, "end": v(-38.2, -1.68) * mm});
            skLineSegment(sketch, "E13.6.20.0", {"start": v(-38.02, -3.92) * mm, "end": v(-40.77, -2.9) * mm});
            skLineSegment(sketch, "E13.1.21.0", {"start": v(-37.91, -4.86) * mm, "end": v(-37.56, -7.07) * mm});
            skLineSegment(sketch, "E13.3.21.0", {"start": v(-40.38, -6.3) * mm, "end": v(-37.91, -4.86) * mm});
            skLineSegment(sketch, "E13.6.21.0", {"start": v(-37.56, -7.07) * mm, "end": v(-40.38, -6.3) * mm});
            skLineSegment(sketch, "E13.1.22.0", {"start": v(-37.37, -8) * mm, "end": v(-36.83, -10.18) * mm});
            skLineSegment(sketch, "E13.3.22.0", {"start": v(-39.7, -9.64) * mm, "end": v(-37.37, -8) * mm});
            skLineSegment(sketch, "E13.6.22.0", {"start": v(-36.83, -10.18) * mm, "end": v(-39.7, -9.64) * mm});
            skLineSegment(sketch, "E13.1.23.0", {"start": v(-36.56, -11.1) * mm, "end": v(-35.84, -13.21) * mm});
            skLineSegment(sketch, "E13.3.23.0", {"start": v(-38.76, -12.92) * mm, "end": v(-36.56, -11.1) * mm});
            skLineSegment(sketch, "E13.6.23.0", {"start": v(-35.84, -13.21) * mm, "end": v(-38.76, -12.92) * mm});
            skLineSegment(sketch, "E13.1.24.0", {"start": v(-35.5, -14.1) * mm, "end": v(-34.6, -16.16) * mm});
            skLineSegment(sketch, "E13.3.24.0", {"start": v(-37.54, -16.1) * mm, "end": v(-35.5, -14.1) * mm});
            skLineSegment(sketch, "E13.6.24.0", {"start": v(-34.6, -16.16) * mm, "end": v(-37.54, -16.1) * mm});
            skLineSegment(sketch, "E13.1.25.0", {"start": v(-34.2, -17.01) * mm, "end": v(-33.13, -18.98) * mm});
            skLineSegment(sketch, "E13.3.25.0", {"start": v(-36.05, -19.18) * mm, "end": v(-34.2, -17.01) * mm});
            skLineSegment(sketch, "E13.6.25.0", {"start": v(-33.13, -18.98) * mm, "end": v(-36.05, -19.18) * mm});
            skLineSegment(sketch, "E13.1.26.0", {"start": v(-32.64, -19.8) * mm, "end": v(-31.42, -21.68) * mm});
            skLineSegment(sketch, "E13.3.26.0", {"start": v(-34.32, -22.12) * mm, "end": v(-32.64, -19.8) * mm});
            skLineSegment(sketch, "E13.6.26.0", {"start": v(-31.42, -21.68) * mm, "end": v(-34.32, -22.12) * mm});
            skLineSegment(sketch, "E13.1.27.0", {"start": v(-30.87, -22.45) * mm, "end": v(-29.49, -24.22) * mm});
            skLineSegment(sketch, "E13.3.27.0", {"start": v(-32.34, -24.9) * mm, "end": v(-30.87, -22.45) * mm});
            skLineSegment(sketch, "E13.6.27.0", {"start": v(-29.49, -24.22) * mm, "end": v(-32.34, -24.9) * mm});
            skLineSegment(sketch, "E13.1.28.0", {"start": v(-28.87, -24.94) * mm, "end": v(-27.35, -26.6) * mm});
            skLineSegment(sketch, "E13.3.28.0", {"start": v(-30.14, -27.5) * mm, "end": v(-28.87, -24.94) * mm});
            skLineSegment(sketch, "E13.6.28.0", {"start": v(-27.35, -26.6) * mm, "end": v(-30.14, -27.5) * mm});
            skLineSegment(sketch, "E13.1.29.0", {"start": v(-26.68, -27.26) * mm, "end": v(-25.03, -28.78) * mm});
            skLineSegment(sketch, "E13.3.29.0", {"start": v(-27.72, -29.92) * mm, "end": v(-26.68, -27.26) * mm});
            skLineSegment(sketch, "E13.6.29.0", {"start": v(-25.03, -28.78) * mm, "end": v(-27.72, -29.92) * mm});
            skLineSegment(sketch, "E13.1.30.0", {"start": v(-24.3, -29.39) * mm, "end": v(-22.53, -30.76) * mm});
            skLineSegment(sketch, "E13.3.30.0", {"start": v(-25.12, -32.12) * mm, "end": v(-24.3, -29.39) * mm});
            skLineSegment(sketch, "E13.6.30.0", {"start": v(-22.53, -30.76) * mm, "end": v(-25.12, -32.12) * mm});
            skLineSegment(sketch, "E13.1.31.0", {"start": v(-21.75, -31.3) * mm, "end": v(-19.87, -32.52) * mm});
            skLineSegment(sketch, "E13.3.31.0", {"start": v(-22.34, -34.1) * mm, "end": v(-21.75, -31.3) * mm});
            skLineSegment(sketch, "E13.6.31.0", {"start": v(-19.87, -32.52) * mm, "end": v(-22.34, -34.1) * mm});
            skLineSegment(sketch, "E13.1.32.0", {"start": v(-19.05, -33) * mm, "end": v(-17.07, -34.06) * mm});
            skLineSegment(sketch, "E13.3.32.0", {"start": v(-19.4, -35.84) * mm, "end": v(-19.05, -33) * mm});
            skLineSegment(sketch, "E13.6.32.0", {"start": v(-17.07, -34.06) * mm, "end": v(-19.4, -35.84) * mm});
            skLineSegment(sketch, "E13.1.33.0", {"start": v(-16.22, -34.47) * mm, "end": v(-14.16, -35.36) * mm});
            skLineSegment(sketch, "E13.3.33.0", {"start": v(-16.33, -37.33) * mm, "end": v(-16.22, -34.47) * mm});
            skLineSegment(sketch, "E13.6.33.0", {"start": v(-14.16, -35.36) * mm, "end": v(-16.33, -37.33) * mm});
            skLineSegment(sketch, "E13.1.34.0", {"start": v(-13.27, -35.7) * mm, "end": v(-11.14, -36.4) * mm});
            skLineSegment(sketch, "E13.3.34.0", {"start": v(-13.14, -38.55) * mm, "end": v(-13.27, -35.7) * mm});
            skLineSegment(sketch, "E13.6.34.0", {"start": v(-11.14, -36.4) * mm, "end": v(-13.14, -38.55) * mm});
            skLineSegment(sketch, "E13.1.35.0", {"start": v(-10.23, -36.67) * mm, "end": v(-8.05, -37.2) * mm});
            skLineSegment(sketch, "E13.3.35.0", {"start": v(-9.87, -39.5) * mm, "end": v(-10.23, -36.67) * mm});
            skLineSegment(sketch, "E13.6.35.0", {"start": v(-8.05, -37.2) * mm, "end": v(-9.87, -39.5) * mm});
            skLineSegment(sketch, "E13.1.36.0", {"start": v(-7.12, -37.39) * mm, "end": v(-4.9, -37.73) * mm});
            skLineSegment(sketch, "E13.3.36.0", {"start": v(-6.52, -40.18) * mm, "end": v(-7.12, -37.39) * mm});
            skLineSegment(sketch, "E13.6.36.0", {"start": v(-4.9, -37.73) * mm, "end": v(-6.52, -40.18) * mm});
            skLineSegment(sketch, "E13.1.37.0", {"start": v(-3.96, -37.84) * mm, "end": v(-1.73, -38) * mm});
            skLineSegment(sketch, "E13.3.37.0", {"start": v(-3.13, -40.57) * mm, "end": v(-3.96, -37.84) * mm});
            skLineSegment(sketch, "E13.6.37.0", {"start": v(-1.73, -38) * mm, "end": v(-3.13, -40.57) * mm});
            skLineSegment(sketch, "E13.1.38.0", {"start": v(-0.78, -38.03) * mm, "end": v(1.46, -38) * mm});
            skLineSegment(sketch, "E13.3.38.0", {"start": v(0.28, -40.68) * mm, "end": v(-0.78, -38.03) * mm});
            skLineSegment(sketch, "E13.6.38.0", {"start": v(1.46, -38) * mm, "end": v(0.28, -40.68) * mm});
            skLineSegment(sketch, "E13.1.39.0", {"start": v(2.41, -37.95) * mm, "end": v(4.64, -37.73) * mm});
            skLineSegment(sketch, "E13.3.39.0", {"start": v(3.69, -40.5) * mm, "end": v(2.41, -37.95) * mm});
            skLineSegment(sketch, "E13.6.39.0", {"start": v(4.64, -37.73) * mm, "end": v(3.69, -40.5) * mm});
            skLineSegment(sketch, "E13.1.40.0", {"start": v(5.58, -37.6) * mm, "end": v(7.79, -37.2) * mm});
            skLineSegment(sketch, "E13.3.40.0", {"start": v(7.07, -40.04) * mm, "end": v(5.58, -37.6) * mm});
            skLineSegment(sketch, "E13.6.40.0", {"start": v(7.79, -37.2) * mm, "end": v(7.07, -40.04) * mm});
            skLineSegment(sketch, "E13.1.41.0", {"start": v(8.72, -37) * mm, "end": v(10.88, -36.4) * mm});
            skLineSegment(sketch, "E13.3.41.0", {"start": v(10.4, -39.3) * mm, "end": v(8.72, -37) * mm});
            skLineSegment(sketch, "E13.6.41.0", {"start": v(10.88, -36.4) * mm, "end": v(10.4, -39.3) * mm});
            skLineSegment(sketch, "E13.1.42.0", {"start": v(11.79, -36.12) * mm, "end": v(13.9, -35.36) * mm});
            skLineSegment(sketch, "E13.3.42.0", {"start": v(13.66, -38.28) * mm, "end": v(11.79, -36.12) * mm});
            skLineSegment(sketch, "E13.6.42.0", {"start": v(13.9, -35.36) * mm, "end": v(13.66, -38.28) * mm});
            skLineSegment(sketch, "E13.1.43.0", {"start": v(14.77, -35) * mm, "end": v(16.8, -34.06) * mm});
            skLineSegment(sketch, "E13.3.43.0", {"start": v(16.82, -37) * mm, "end": v(14.77, -35) * mm});
            skLineSegment(sketch, "E13.6.43.0", {"start": v(16.8, -34.06) * mm, "end": v(16.82, -37) * mm});
            skLineSegment(sketch, "E13.1.44.0", {"start": v(17.65, -33.63) * mm, "end": v(19.6, -32.52) * mm});
            skLineSegment(sketch, "E13.3.44.0", {"start": v(19.86, -35.44) * mm, "end": v(17.65, -33.63) * mm});
            skLineSegment(sketch, "E13.6.44.0", {"start": v(19.6, -32.52) * mm, "end": v(19.86, -35.44) * mm});
            skLineSegment(sketch, "E13.1.45.0", {"start": v(20.41, -32.02) * mm, "end": v(22.26, -30.76) * mm});
            skLineSegment(sketch, "E13.3.45.0", {"start": v(22.76, -33.65) * mm, "end": v(20.41, -32.02) * mm});
            skLineSegment(sketch, "E13.6.45.0", {"start": v(22.26, -30.76) * mm, "end": v(22.76, -33.65) * mm});
            skLineSegment(sketch, "E13.1.46.0", {"start": v(23.02, -30.19) * mm, "end": v(24.76, -28.78) * mm});
            skLineSegment(sketch, "E13.3.46.0", {"start": v(25.5, -31.61) * mm, "end": v(23.02, -30.19) * mm});
            skLineSegment(sketch, "E13.6.46.0", {"start": v(24.76, -28.78) * mm, "end": v(25.5, -31.61) * mm});
            skLineSegment(sketch, "E13.1.47.0", {"start": v(25.48, -28.15) * mm, "end": v(27.09, -26.6) * mm});
            skLineSegment(sketch, "E13.3.47.0", {"start": v(28.06, -29.36) * mm, "end": v(25.48, -28.15) * mm});
            skLineSegment(sketch, "E13.6.47.0", {"start": v(27.09, -26.6) * mm, "end": v(28.06, -29.36) * mm});
            skLineSegment(sketch, "E13.1.48.0", {"start": v(27.75, -25.9) * mm, "end": v(29.22, -24.22) * mm});
            skLineSegment(sketch, "E13.3.48.0", {"start": v(30.43, -26.9) * mm, "end": v(27.75, -25.9) * mm});
            skLineSegment(sketch, "E13.6.48.0", {"start": v(29.22, -24.22) * mm, "end": v(30.43, -26.9) * mm});
            skLineSegment(sketch, "E13.1.49.0", {"start": v(29.82, -23.48) * mm, "end": v(31.15, -21.68) * mm});
            skLineSegment(sketch, "E13.3.49.0", {"start": v(32.57, -24.24) * mm, "end": v(29.82, -23.48) * mm});
            skLineSegment(sketch, "E13.6.49.0", {"start": v(31.15, -21.68) * mm, "end": v(32.57, -24.24) * mm});
            skLineSegment(sketch, "E14.1.50.0", {"start": v(31.69, -20.9) * mm, "end": v(32.86, -18.98) * mm});
            skLineSegment(sketch, "E14.3.50.0", {"start": v(34.5, -21.42) * mm, "end": v(31.69, -20.9) * mm});
            skLineSegment(sketch, "E14.6.50.0", {"start": v(32.86, -18.98) * mm, "end": v(34.5, -21.42) * mm});
            skLineSegment(sketch, "E14.1.51.0", {"start": v(33.33, -18.16) * mm, "end": v(34.34, -16.16) * mm});
            skLineSegment(sketch, "E14.3.51.0", {"start": v(36.17, -18.45) * mm, "end": v(33.33, -18.16) * mm});
            skLineSegment(sketch, "E14.6.51.0", {"start": v(34.34, -16.16) * mm, "end": v(36.17, -18.45) * mm});
            skLineSegment(sketch, "E14.1.52.0", {"start": v(34.74, -15.3) * mm, "end": v(35.58, -13.21) * mm});
            skLineSegment(sketch, "E14.3.52.0", {"start": v(37.6, -15.34) * mm, "end": v(34.74, -15.3) * mm});
            skLineSegment(sketch, "E14.6.52.0", {"start": v(35.58, -13.21) * mm, "end": v(37.6, -15.34) * mm});
            skLineSegment(sketch, "E14.1.53.0", {"start": v(35.9, -12.32) * mm, "end": v(36.56, -10.18) * mm});
            skLineSegment(sketch, "E14.3.53.0", {"start": v(38.75, -12.13) * mm, "end": v(35.9, -12.32) * mm});
            skLineSegment(sketch, "E14.6.53.0", {"start": v(36.56, -10.18) * mm, "end": v(38.75, -12.13) * mm});
            skLineSegment(sketch, "E14.1.54.0", {"start": v(36.8, -9.26) * mm, "end": v(37.3, -7.07) * mm});
            skLineSegment(sketch, "E14.3.54.0", {"start": v(39.63, -8.84) * mm, "end": v(36.8, -9.26) * mm});
            skLineSegment(sketch, "E14.6.54.0", {"start": v(37.3, -7.07) * mm, "end": v(39.63, -8.84) * mm});
            skLineSegment(sketch, "E14.1.55.0", {"start": v(37.46, -6.14) * mm, "end": v(37.76, -3.92) * mm});
            skLineSegment(sketch, "E14.3.55.0", {"start": v(40.24, -5.48) * mm, "end": v(37.46, -6.14) * mm});
            skLineSegment(sketch, "E14.6.55.0", {"start": v(37.76, -3.92) * mm, "end": v(40.24, -5.48) * mm});
            skLineSegment(sketch, "E14.1.56.0", {"start": v(37.85, -2.97) * mm, "end": v(37.96, -0.73) * mm});
            skLineSegment(sketch, "E14.3.56.0", {"start": v(40.56, -2.08) * mm, "end": v(37.85, -2.97) * mm});
            skLineSegment(sketch, "E14.6.56.0", {"start": v(37.96, -0.73) * mm, "end": v(40.56, -2.08) * mm});
            skLineSegment(sketch, "E14.1.57.0", {"start": v(37.97, 0.22) * mm, "end": v(37.9, 2.46) * mm});
            skLineSegment(sketch, "E14.3.57.0", {"start": v(40.6, 1.33) * mm, "end": v(37.97, 0.22) * mm});
            skLineSegment(sketch, "E14.6.57.0", {"start": v(37.9, 2.46) * mm, "end": v(40.6, 1.33) * mm});
            skLineSegment(sketch, "E14.1.58.0", {"start": v(37.82, 3.4) * mm, "end": v(37.56, 5.63) * mm});
            skLineSegment(sketch, "E14.3.58.0", {"start": v(40.35, 4.74) * mm, "end": v(37.82, 3.4) * mm});
            skLineSegment(sketch, "E14.6.58.0", {"start": v(37.56, 5.63) * mm, "end": v(40.35, 4.74) * mm});
            skLineSegment(sketch, "E14.1.59.0", {"start": v(37.4, 6.57) * mm, "end": v(36.96, 8.77) * mm});
            skLineSegment(sketch, "E14.3.59.0", {"start": v(39.82, 8.1) * mm, "end": v(37.4, 6.57) * mm});
            skLineSegment(sketch, "E14.6.59.0", {"start": v(36.96, 8.77) * mm, "end": v(39.82, 8.1) * mm});
            skLineSegment(sketch, "E14.1.60.0", {"start": v(36.73, 9.69) * mm, "end": v(36.1, 11.84) * mm});
            skLineSegment(sketch, "E14.3.60.0", {"start": v(39, 11.42) * mm, "end": v(36.73, 9.69) * mm});
            skLineSegment(sketch, "E14.6.60.0", {"start": v(36.1, 11.84) * mm, "end": v(39, 11.42) * mm});
            skLineSegment(sketch, "E14.1.61.0", {"start": v(35.8, 12.74) * mm, "end": v(35, 14.83) * mm});
            skLineSegment(sketch, "E14.3.61.0", {"start": v(37.92, 14.66) * mm, "end": v(35.8, 12.74) * mm});
            skLineSegment(sketch, "E14.6.61.0", {"start": v(35, 14.83) * mm, "end": v(37.92, 14.66) * mm});
            skLineSegment(sketch, "E14.1.62.0", {"start": v(34.61, 15.7) * mm, "end": v(33.63, 17.72) * mm});
            skLineSegment(sketch, "E14.3.62.0", {"start": v(36.56, 17.79) * mm, "end": v(34.61, 15.7) * mm});
            skLineSegment(sketch, "E14.6.62.0", {"start": v(33.63, 17.72) * mm, "end": v(36.56, 17.79) * mm});
            skLineSegment(sketch, "E14.1.63.0", {"start": v(33.18, 18.55) * mm, "end": v(32.04, 20.48) * mm});
            skLineSegment(sketch, "E14.3.63.0", {"start": v(34.95, 20.8) * mm, "end": v(33.18, 18.55) * mm});
            skLineSegment(sketch, "E14.6.63.0", {"start": v(32.04, 20.48) * mm, "end": v(34.95, 20.8) * mm});
            skLineSegment(sketch, "E14.1.64.0", {"start": v(31.52, 21.28) * mm, "end": v(30.22, 23.1) * mm});
            skLineSegment(sketch, "E14.3.64.0", {"start": v(33.1, 23.66) * mm, "end": v(31.52, 21.28) * mm});
            skLineSegment(sketch, "E14.6.64.0", {"start": v(30.22, 23.1) * mm, "end": v(33.1, 23.66) * mm});
            skLineSegment(sketch, "E14.1.65.0", {"start": v(29.63, 23.85) * mm, "end": v(28.18, 25.56) * mm});
            skLineSegment(sketch, "E14.3.65.0", {"start": v(31, 26.36) * mm, "end": v(29.63, 23.85) * mm});
            skLineSegment(sketch, "E14.6.65.0", {"start": v(28.18, 25.56) * mm, "end": v(31, 26.36) * mm});
            skLineSegment(sketch, "E14.1.66.0", {"start": v(27.54, 26.26) * mm, "end": v(25.95, 27.84) * mm});
            skLineSegment(sketch, "E14.3.66.0", {"start": v(28.7, 28.87) * mm, "end": v(27.54, 26.26) * mm});
            skLineSegment(sketch, "E14.6.66.0", {"start": v(25.95, 27.84) * mm, "end": v(28.7, 28.87) * mm});
            skLineSegment(sketch, "E14.1.67.0", {"start": v(25.25, 28.48) * mm, "end": v(23.53, 29.92) * mm});
            skLineSegment(sketch, "E14.3.67.0", {"start": v(26.18, 31.18) * mm, "end": v(25.25, 28.48) * mm});
            skLineSegment(sketch, "E14.6.67.0", {"start": v(23.53, 29.92) * mm, "end": v(26.18, 31.18) * mm});
            skLineSegment(sketch, "E14.1.68.0", {"start": v(22.78, 30.5) * mm, "end": v(20.95, 31.8) * mm});
            skLineSegment(sketch, "E14.3.68.0", {"start": v(23.49, 33.27) * mm, "end": v(22.78, 30.5) * mm});
            skLineSegment(sketch, "E14.6.68.0", {"start": v(20.95, 31.8) * mm, "end": v(23.49, 33.27) * mm});
            skLineSegment(sketch, "E14.1.69.0", {"start": v(20.15, 32.32) * mm, "end": v(18.22, 33.45) * mm});
            skLineSegment(sketch, "E14.3.69.0", {"start": v(20.62, 35.13) * mm, "end": v(20.15, 32.32) * mm});
            skLineSegment(sketch, "E14.6.69.0", {"start": v(18.22, 33.45) * mm, "end": v(20.62, 35.13) * mm});
            skLineSegment(sketch, "E14.1.70.0", {"start": v(17.38, 33.9) * mm, "end": v(15.36, 34.87) * mm});
            skLineSegment(sketch, "E14.3.70.0", {"start": v(17.62, 36.75) * mm, "end": v(17.38, 33.9) * mm});
            skLineSegment(sketch, "E14.6.70.0", {"start": v(15.36, 34.87) * mm, "end": v(17.62, 36.75) * mm});
            skLineSegment(sketch, "E14.1.71.0", {"start": v(14.5, 35.25) * mm, "end": v(12.4, 36.05) * mm});
            skLineSegment(sketch, "E14.3.71.0", {"start": v(14.48, 38.1) * mm, "end": v(14.5, 35.25) * mm});
            skLineSegment(sketch, "E14.6.71.0", {"start": v(12.4, 36.05) * mm, "end": v(14.48, 38.1) * mm});
            skLineSegment(sketch, "E14.1.72.0", {"start": v(11.5, 36.35) * mm, "end": v(9.34, 36.97) * mm});
            skLineSegment(sketch, "E14.3.72.0", {"start": v(11.25, 39.2) * mm, "end": v(11.5, 36.35) * mm});
            skLineSegment(sketch, "E14.6.72.0", {"start": v(9.34, 36.97) * mm, "end": v(11.25, 39.2) * mm});
            skLineSegment(sketch, "E14.1.73.0", {"start": v(8.42, 37.2) * mm, "end": v(6.22, 37.63) * mm});
            skLineSegment(sketch, "E14.3.73.0", {"start": v(7.94, 40) * mm, "end": v(8.42, 37.2) * mm});
            skLineSegment(sketch, "E14.6.73.0", {"start": v(6.22, 37.63) * mm, "end": v(7.94, 40) * mm});
            skLineSegment(sketch, "E14.1.74.0", {"start": v(5.28, 37.78) * mm, "end": v(3.06, 38.03) * mm});
            skLineSegment(sketch, "E14.3.74.0", {"start": v(4.57, 40.54) * mm, "end": v(5.28, 37.78) * mm});
            skLineSegment(sketch, "E14.6.74.0", {"start": v(3.06, 38.03) * mm, "end": v(4.57, 40.54) * mm});
            skSolve(sketch);
        }
        {
            var Q0;
            Q0 = qSketchRegion(id + "F4", true);
            extrude(context, id + "F5", {"entities" : qUnion([Q0]), "operationType" : NewBodyOperationType.ADD, "depth" : 3.17 * mm, "offsetDistance" : 25.4 * mm});
        }
    });
